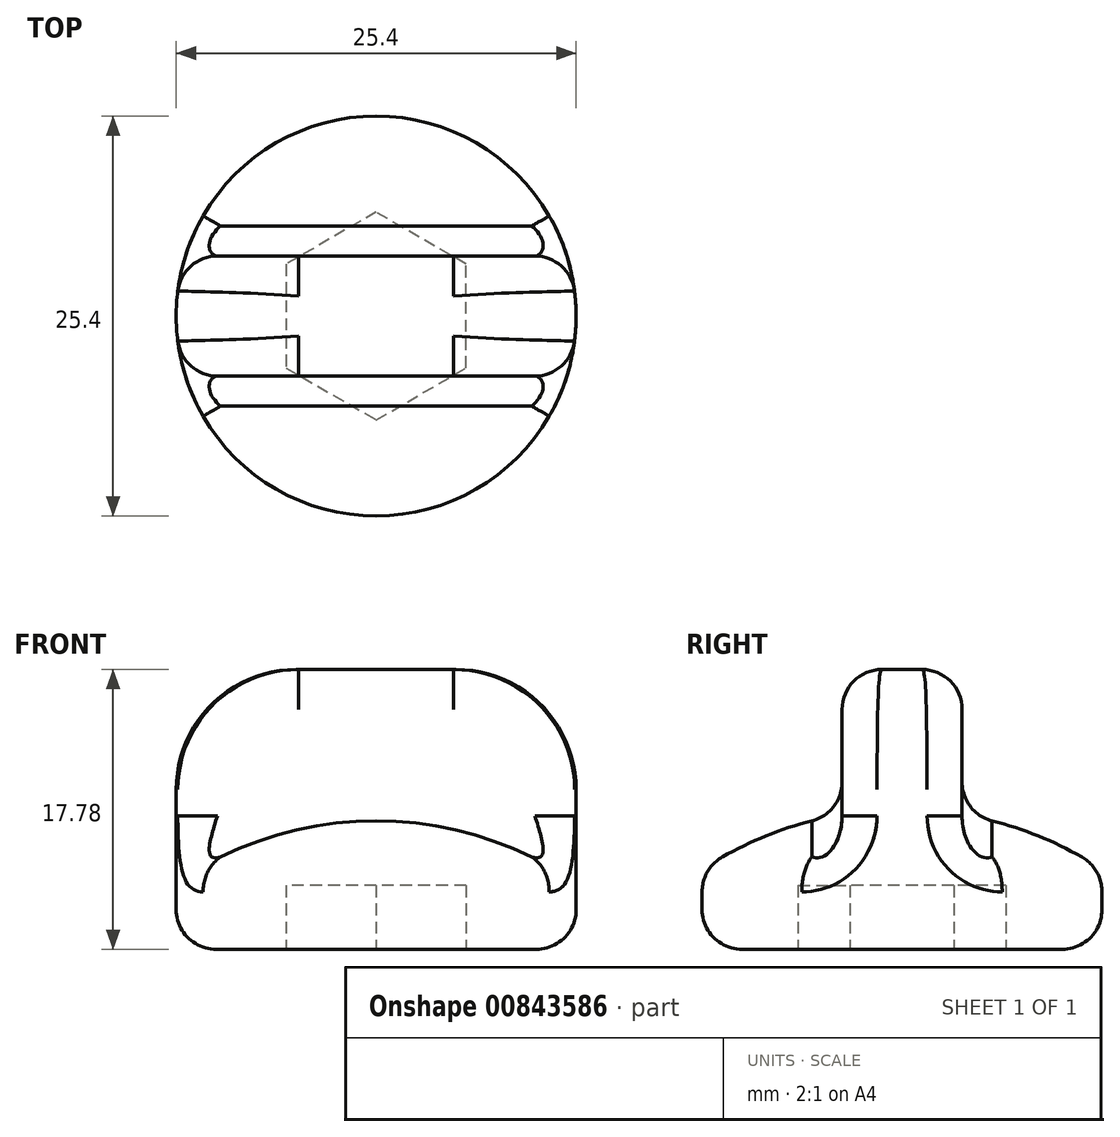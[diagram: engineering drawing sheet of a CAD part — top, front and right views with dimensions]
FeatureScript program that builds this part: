
annotation { "Feature Type Name" : "Feature", "Feature Type Description" : "" }
export const myFeature = defineFeature(function(context is Context, id is Id, definition is map)
    precondition{}
    {
        {
            var Q0;
            Q0=qCreatedBy(makeId("Top.planeOp"),FACE);
            var sketch = newSketch(context, id + "F0", { "sketchPlane" : qUnion([Q0])});
            skCircle(sketch, "E0", {"center": v(0, 0) * mm, "radius": 12.7 * mm});
            skSolve(sketch);
        }
        {
            var Q0;
            Q0=qCreatedBy(makeId("Front.planeOp"),FACE);
            var sketch = newSketch(context, id + "F1", { "sketchPlane" : qUnion([Q0])});
            skArc(sketch, "E1", {"start": v(0, 3.8) * mm, "mid": v(-6.63, 2.84) * mm, "end": v(-12.7, 0) * mm});
            skLineSegment(sketch, "E2", {"start": v(0, 3.81) * mm, "end": v(-27.27, 3.81) * mm, "construction": true});
            skLineSegment(sketch, "E3", {"start": v(-12.7, 0) * mm, "end": v(0, 0) * mm});
            skLineSegment(sketch, "E4", {"start": v(0, 0) * mm, "end": v(0, 3.8) * mm});
            skSolve(sketch);
        }
        {
            var Q0;
            Q0 = qSketchRegion(id + "F0", true);
            extrude(context, id + "F2", {"entities" : qUnion([Q0]), "oppositeDirection" : true, "depth" : 5.08 * mm, "offsetDistance" : 25.4 * mm});
        }
        {
            var Q0;
            Q0 = qSketchRegion(id + "F1", true);
            var Q1;
            Q1=sQuery(id+"F1.wireOp",EDGE,"E4");
            revolve(context, id + "F3", {"operationType" : NewBodyOperationType.ADD, "surfaceOperationType" : NewSurfaceOperationType.NEW, "entities" : qUnion([Q0]), "axis" : qUnion([Q1]), "revolveType" : RevolveType.FULL});
        }
        {
            var Q0;
            Q0=makeQuery(id+"F2.opExtrude","CAP_EDGE",EDGE,{"disambiguationData":[OSD([sQuery(id+"F0.wireOp",EDGE,"E0")])],"isStart":false});
            fillet(context, id + "F4", {"entities" : qUnion([Q0]), "radius" : 2.54 * mm, "tangentPropagation" : true, "allowEdgeOverflow" : false});
        }
        {
            var Q0;
            Q0=qCreatedBy(makeId("Top.planeOp"),FACE);
            var sketch = newSketch(context, id + "F5", { "sketchPlane" : qUnion([Q0])});
            skLineSegment(sketch, "E5.bottom", {"start": v(-12.12, 3.81) * mm, "end": v(12.12, 3.81) * mm});
            skLineSegment(sketch, "E5.top", {"start": v(-12.12, -3.81) * mm, "end": v(12.12, -3.81) * mm});
            skArc(sketch, "E6", {"start": v(12.12, -3.81) * mm, "mid": v(12.7, 0) * mm, "end": v(12.12, 3.81) * mm});
            skArc(sketch, "E7", {"start": v(-12.12, 3.81) * mm, "mid": v(-12.7, 0) * mm, "end": v(-12.12, -3.81) * mm});
            skSolve(sketch);
        }
        {
            var Q0;
            Q0 = qSketchRegion(id + "F5", true);
            extrude(context, id + "F6", {"entities" : qUnion([Q0]), "operationType" : NewBodyOperationType.ADD, "depth" : 12.7 * mm, "offsetDistance" : 25.4 * mm});
        }
        {
            var Q0;
            Q0=makeQuery(id+"F6.boolean.opBoolean","INTERSECT",EDGE,{"derivedFrom":[makeQuery(id+"F3.opRevolve","SWEPT_FACE",FACE,{"disambiguationData":[OSD([sQuery(id+"F1.wireOp",EDGE,"E1")])]}),makeQuery(id+"F6.opExtrude","SWEPT_FACE",FACE,{"disambiguationData":[OSD([sQuery(id+"F5.wireOp",EDGE,"E5.bottom")])]})]});
            var Q1;
            Q1=makeQuery(id+"F6.boolean.opBoolean","INTERSECT",EDGE,{"derivedFrom":[makeQuery(id+"F3.opRevolve","SWEPT_FACE",FACE,{"disambiguationData":[OSD([sQuery(id+"F1.wireOp",EDGE,"E1")])]}),makeQuery(id+"F6.opExtrude","SWEPT_FACE",FACE,{"disambiguationData":[OSD([sQuery(id+"F5.wireOp",EDGE,"E5.top")])]})]});
            fillet(context, id + "F7", {"entities" : qUnion([Q0, Q1]), "radius" : 2.54 * mm, "tangentPropagation" : true, "allowEdgeOverflow" : false});
        }
        {
            var Q0;
            Q0=makeQuery(id+"F6.opExtrude","CAP_EDGE",EDGE,{"disambiguationData":[OSD([sQuery(id+"F5.wireOp",EDGE,"E5.bottom")])],"isStart":false});
            var Q1;
            Q1=makeQuery(id+"F6.opExtrude","CAP_EDGE",EDGE,{"disambiguationData":[OSD([sQuery(id+"F5.wireOp",EDGE,"E5.top")])],"isStart":false});
            fillet(context, id + "F8", {"entities" : qUnion([Q0, Q1]), "radius" : 2.54 * mm, "tangentPropagation" : true, "allowEdgeOverflow" : false});
        }
        {
            var Q0;
            Q0=makeQuery(id+"F6.opExtrude","CAP_EDGE",EDGE,{"disambiguationData":[OSD([sQuery(id+"F5.wireOp",EDGE,"E7")])],"isStart":false});
            var Q1;
            Q1=makeQuery(id+"F6.opExtrude","CAP_EDGE",EDGE,{"disambiguationData":[OSD([sQuery(id+"F5.wireOp",EDGE,"E6")])],"isStart":false});
            fillet(context, id + "F9", {"entities" : qUnion([Q0, Q1]), "radius" : 7.62 * mm, "allowEdgeOverflow" : false});
        }
        {
            var Q0;
            Q0=makeQuery(id+"F2.opExtrude","CAP_FACE",FACE,{"disambiguationData":[OSD([sQuery(id+"F0.wireOp",EDGE,"E0")])],"isStart":false});
            var sketch = newSketch(context, id + "F10", { "sketchPlane" : qUnion([Q0])});
            skCircle(sketch, "E8.cCircle", {"center": v(0, 0) * mm, "radius": 5.72 * mm, "construction": true});
            skLineSegment(sketch, "E8.0", {"start": v(-5.71, -3.3) * mm, "end": v(-5.71, 3.3) * mm});
            skLineSegment(sketch, "E8.1", {"start": v(-5.71, 3.3) * mm, "end": v(0, 6.6) * mm});
            skLineSegment(sketch, "E8.2", {"start": v(0, 6.6) * mm, "end": v(5.71, 3.3) * mm});
            skLineSegment(sketch, "E8.3", {"start": v(5.71, 3.3) * mm, "end": v(5.71, -3.3) * mm});
            skLineSegment(sketch, "E8.4", {"start": v(5.71, -3.3) * mm, "end": v(0, -6.6) * mm});
            skLineSegment(sketch, "E8.5", {"start": v(0, -6.6) * mm, "end": v(-5.71, -3.3) * mm});
            skPoint(sketch, "E8.0.midPoint", {"position": v(-5.71, 0) * mm});
            skSolve(sketch);
        }
        {
            var Q0;
            Q0 = qSketchRegion(id + "F10", true);
            extrude(context, id + "F11", {"entities" : qUnion([Q0]), "operationType" : NewBodyOperationType.REMOVE, "oppositeDirection" : true, "depth" : 4.06 * mm, "offsetDistance" : 25.4 * mm});
        }
        {
            var Q0;
            Q0=makeQuery(id+"F3.boolean.opBoolean","MERGE",EDGE,{"derivedFrom":[makeQuery(id+"F2.opExtrude","CAP_EDGE",EDGE,{"disambiguationData":[OSD([sQuery(id+"F0.wireOp",EDGE,"E0")])],"isStart":true}),makeQuery(id+"F3.opRevolve","SWEPT_EDGE",EDGE,{"disambiguationData":[OSD([sQuery(id+"F1.wireOp",EDGE,"E1"),sQuery(id+"F1.wireOp",EDGE,"E3")])]})]});
            fillet(context, id + "F12", {"entities" : qUnion([Q0]), "radius" : 2.54 * mm, "tangentPropagation" : true, "allowEdgeOverflow" : false});
        }
    });
